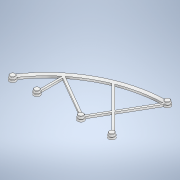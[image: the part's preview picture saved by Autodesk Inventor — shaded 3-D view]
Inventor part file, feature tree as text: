
AUTODESK INVENTOR PART (.ipt)
format: ipt  version: 2022.1 (Build 261234000, 234)  size: 225,792 bytes
history: native  units: in
note: dims shown in document units (in); Inventor stores cm internally (conversion verified against a paired STEP export)
features: extrude x4, sketch x4, fillet x2
ambient origin geometry x8: Origin, YZ Plane, XZ Plane, XY Plane, X Axis, Y Axis, Z Axis, Center Point
bodies: Solid1 (feature_tree)
feature tree (10):
  extrude  "Extrusion1"  Depth=5.9843in
  extrude  "Extrusion2"  TaperAngle=0.0deg  [1 undecoded]
  extrude  "Circular_Mounts"  Depth=0.125in
  extrude  "Inserts"  Depth=0.1181in
  fillet  "Fillet2"  Radius=0.25in
  fillet  "Fillet3"  Radius=0.1387in
  sketch  "Sketch1"  dims[d0=5.9843in d1=5.9843in]
  sketch  "Sketch2"  dims[d2=3.937in d3=0.0in]
  sketch  "Sketch3"  dims[d4=45.0deg d8=0.125in]
  sketch  "Sketch4"  dims[d9=0.125in d10=0.25in d11=0.25in d12=0.1387in d13=0.1387in d14=0.1181in d15=0.0in d16=7.874in d17=7.874in d18=0.125in d19=0.0in d20=0.3937in d21=0.1181in d22=0.0in d23=0.3189in d24=0.1575in d25=0.0in d27=0.0197in d28=0.0787in d29=0.1181in d30=6.1923in]
note: 1 required parameter value undecoded (feature->parameter linkage not recoverable at this tier; creation-order binding heuristic only, values carry confidence <= 0.55)
